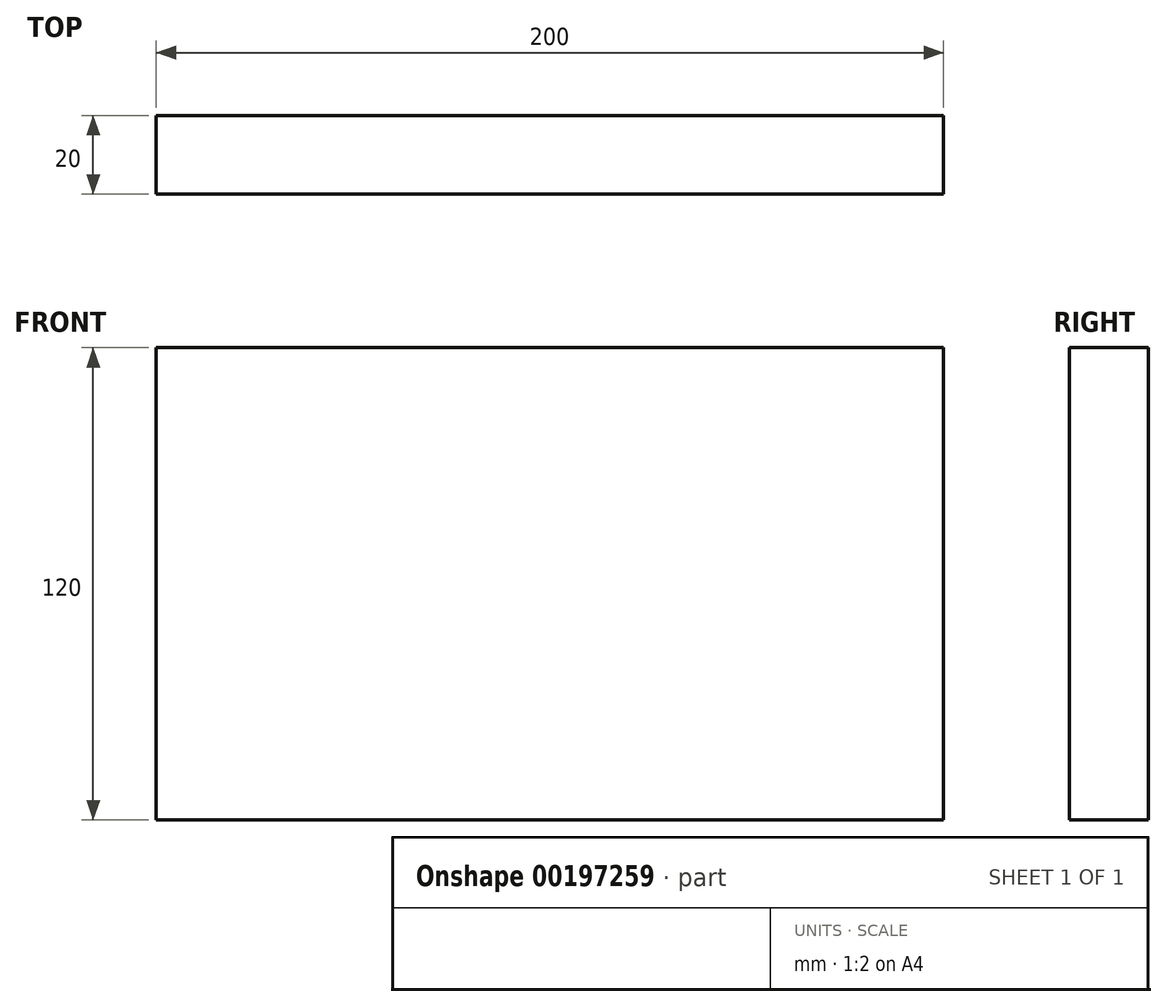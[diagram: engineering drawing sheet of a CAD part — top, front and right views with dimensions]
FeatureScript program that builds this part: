
annotation { "Feature Type Name" : "Feature", "Feature Type Description" : "" }
export const myFeature = defineFeature(function(context is Context, id is Id, definition is map)
    precondition{}
    {
        {
            var Q0;
            Q0=qCreatedBy(makeId("Front.planeOp"),FACE);
            var sketch = newSketch(context, id + "F0", { "sketchPlane" : qUnion([Q0])});
            skLineSegment(sketch, "E0.bottom", {"start": v(100, -60) * mm, "end": v(-100, -60) * mm});
            skLineSegment(sketch, "E0.top", {"start": v(100, 60) * mm, "end": v(-100, 60) * mm});
            skLineSegment(sketch, "E0.left", {"start": v(100, -60) * mm, "end": v(100, 60) * mm});
            skLineSegment(sketch, "E0.right", {"start": v(-100, -60) * mm, "end": v(-100, 60) * mm});
            skPoint(sketch, "E0.middle", {"position": v(0, 0) * mm});
            skSolve(sketch);
        }
        {
            var Q0;
            Q0 = qSketchRegion(id + "F0", true);
            extrude(context, id + "F1", {"entities" : qUnion([Q0]), "oppositeDirection" : true, "depth" : 20 * mm});
        }
    });
